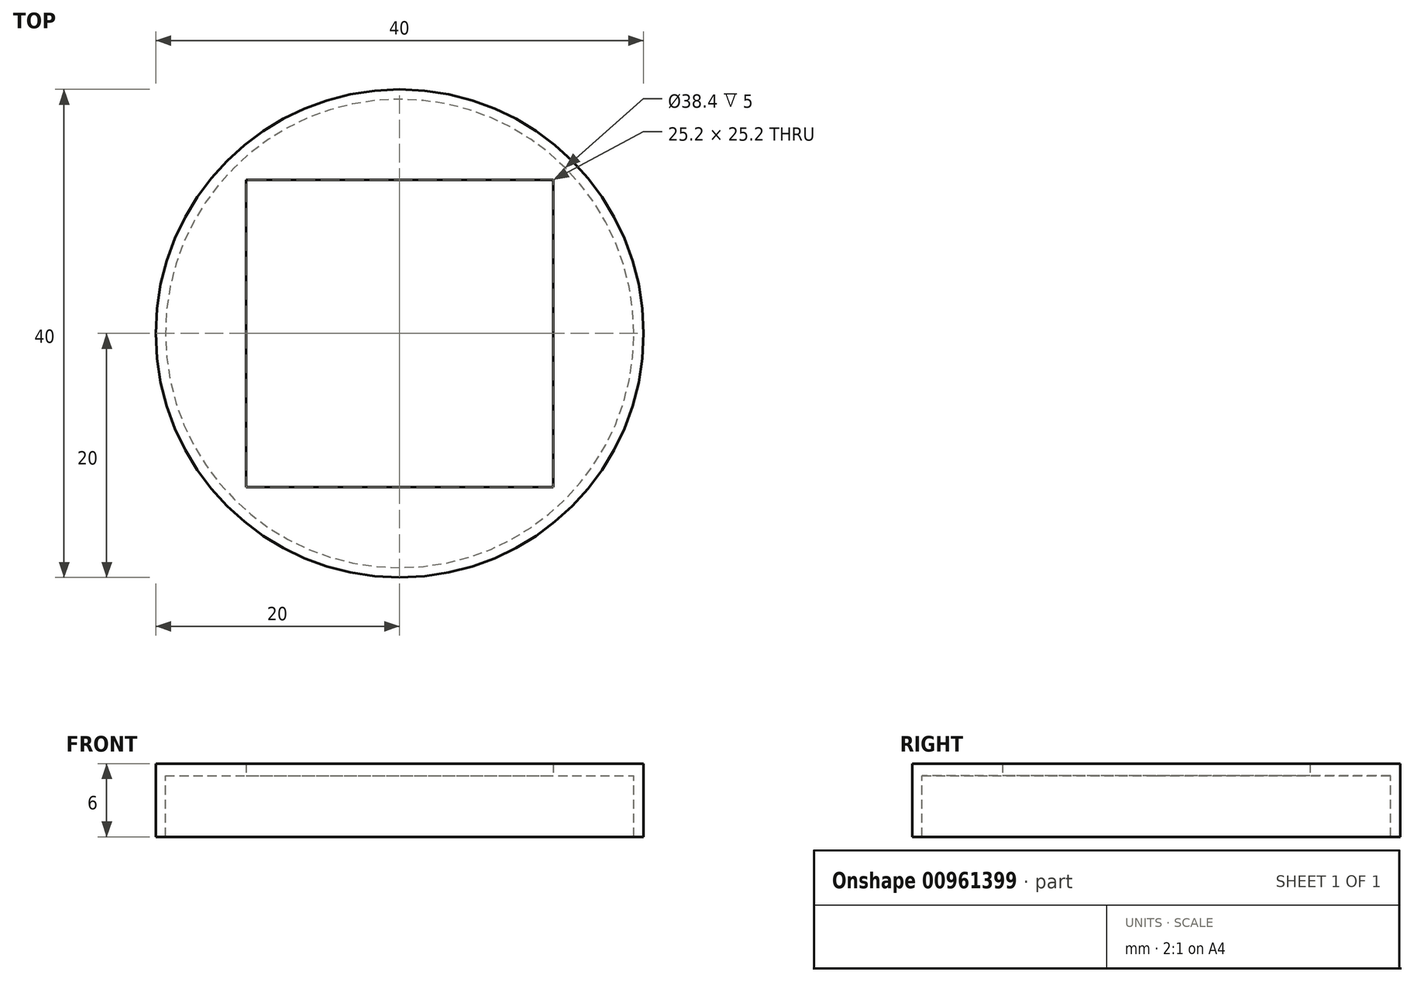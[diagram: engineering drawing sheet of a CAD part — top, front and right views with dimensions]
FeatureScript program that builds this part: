
annotation { "Feature Type Name" : "Feature", "Feature Type Description" : "" }
export const myFeature = defineFeature(function(context is Context, id is Id, definition is map)
    precondition{}
    {
        {
            var Q0;
            Q0=qCreatedBy(makeId("Top.planeOp"),FACE);
            var sketch = newSketch(context, id + "F0", { "sketchPlane" : qUnion([Q0])});
            skCircle(sketch, "E0", {"center": v(0, 0) * mm, "radius": 20 * mm});
            skLineSegment(sketch, "E1.bottom", {"start": v(-12.6, 12.6) * mm, "end": v(12.6, 12.6) * mm});
            skLineSegment(sketch, "E1.top", {"start": v(-12.6, -12.6) * mm, "end": v(12.6, -12.6) * mm});
            skLineSegment(sketch, "E1.left", {"start": v(-12.6, 12.6) * mm, "end": v(-12.6, -12.6) * mm});
            skLineSegment(sketch, "E1.right", {"start": v(12.6, 12.6) * mm, "end": v(12.6, -12.6) * mm});
            skPoint(sketch, "E2", {"position": v(12.6, 0) * mm});
            skPoint(sketch, "E3", {"position": v(0, 12.6) * mm});
            skSolve(sketch);
        }
        {
            var Q0;
            Q0=makeQuery(id+"F0.imprint","IMPRINT",FACE,{"disambiguationData":[TD([[makeQuery(id+"F0.imprint","IMPRINT",EDGE,{"derivedFrom":sQuery(id+"F0.wireOp",EDGE,"E0")}),1.0]])]});
            extrude(context, id + "F1", {"entities" : qUnion([Q0]), "depth" : 1 * mm, "offsetDistance" : 25 * mm});
        }
        {
            var Q0;
            Q0=makeQuery(id+"F1.opExtrude","CAP_FACE",FACE,{"disambiguationData":[OSD([sQuery(id+"F0.wireOp",EDGE,"E0"),sQuery(id+"F0.wireOp",EDGE,"E1.bottom"),sQuery(id+"F0.wireOp",EDGE,"E1.top"),sQuery(id+"F0.wireOp",EDGE,"E1.left"),sQuery(id+"F0.wireOp",EDGE,"E1.right")])],"isStart":true});
            var Q1;
            Q1=makeQuery(id+"F1.opExtrude","CAP_FACE",FACE,{"disambiguationData":[OSD([sQuery(id+"F0.wireOp",EDGE,"E0"),sQuery(id+"F0.wireOp",EDGE,"E1.bottom"),sQuery(id+"F0.wireOp",EDGE,"E1.top"),sQuery(id+"F0.wireOp",EDGE,"E1.left"),sQuery(id+"F0.wireOp",EDGE,"E1.right")])],"isStart":true});
            var Q2;
            Q2=makeQuery(id+"F1.opExtrude","CAP_FACE",FACE,{"disambiguationData":[OSD([sQuery(id+"F0.wireOp",EDGE,"E0"),sQuery(id+"F0.wireOp",EDGE,"E1.bottom"),sQuery(id+"F0.wireOp",EDGE,"E1.top"),sQuery(id+"F0.wireOp",EDGE,"E1.left"),sQuery(id+"F0.wireOp",EDGE,"E1.right")])],"isStart":true});
            var sketch = newSketch(context, id + "F2", { "sketchPlane" : qUnion([Q0, Q1, Q2])});
            skCircle(sketch, "E4", {"center": v(0, 0) * mm, "radius": 20 * mm});
            skCircle(sketch, "E5", {"center": v(0, 0) * mm, "radius": 19.2 * mm});
            skSolve(sketch);
        }
        {
            var Q0;
            Q0 = qSketchRegion(id + "F2", true);
            extrude(context, id + "F3", {"entities" : qUnion([Q0]), "operationType" : NewBodyOperationType.ADD, "depth" : 5 * mm, "offsetDistance" : 25 * mm});
        }
    });
